# Revit family: All-Lite_EFD-635_R17
name_source: partatom
category: Mechanical Equipment
units: mm (PartAtom-declared; Revit-internal decimal feet)

## family parameters
Cut with Voids When Loaded = No
Host = Face
Part Type = Normal
Room Calculation Point = No
Round Connector Dimension = Use Diameter
Shared = No

## types (2) — shared parameters
Air Volume Delivered = 12,138 cfm
Assembly Code = B3020300
Blades = 35° x 0.081'' thick drainable style.
Default Elevation = 0"
Depth = 6"
Description = The EFD-635 drainable blade louver is designed to prevent
water penetration in non-wind-driven rain applications by
collecting water in frame and blade gutters and channeling it into
downspouts and away from airflow paths. The EFD-635 is
available in a wide array of anodized and painted finishes
including custom color matching.
Design Load = 30 psf
Frame = 6'' deep x 0.081'' thick channel.
Free Area (48" x 48") = 9.7 ft² 60.7%
Free Area Velocity = 1250 fpm
Manufacturer = Pottorff
Material = Mill finish 6063-T5 extruded aluminum.
Maximum Size = 60'' x 120''
Minimum Size = 4.5'' x 8'
Model = EFD-635
Modeled By = Commense Studio
Mullion = Visible
Pressure Loss = .20 in. wg
Screen = 1/2'' x 0.063'' expanded and flattened aluminum.
Velocity @ .15 in.wg. Pressure Loss = 1099 fpm

## per-type parameters (varying)
| type | Array Control 1 | Array Control 2 | Blade Width | Height | Height Control | Product URL | URL | Width | Width Control |
| 60" x 120" | 27 | 27 | 58" | 120" | 120" | https://www.alllite.com | https://www.alllite.com | 60" | 60" |
| 36" x 48" | 9 | 9 | 34" | 48" | 48" |  | https://www.pottorff.com | 36" | 36" |

## geometry (parser evidence)
native form markers: Blend x4, Sweep x7
no freeform markers — native parametric forms only
